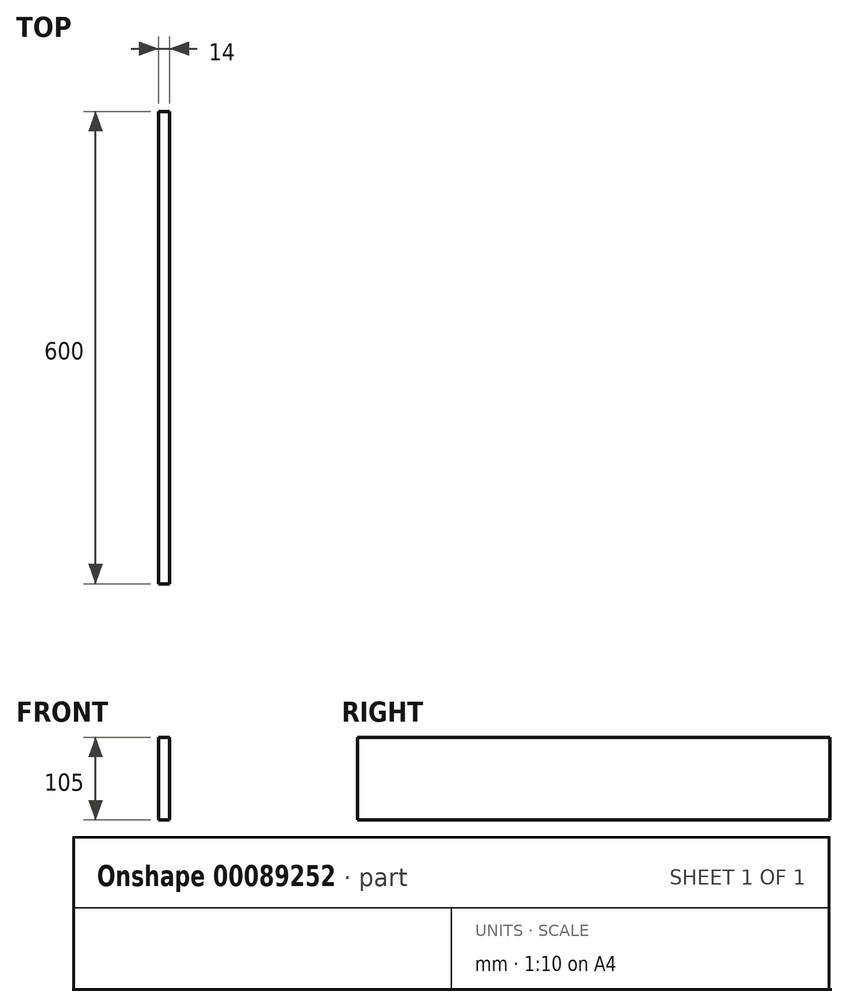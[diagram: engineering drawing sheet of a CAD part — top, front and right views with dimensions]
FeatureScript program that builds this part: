
annotation { "Feature Type Name" : "Feature", "Feature Type Description" : "" }
export const myFeature = defineFeature(function(context is Context, id is Id, definition is map)
    precondition{}
    {
        {
            var Q0;
            Q0=qCreatedBy(makeId("Front.planeOp"),FACE);
            var sketch = newSketch(context, id + "F0", { "sketchPlane" : qUnion([Q0])});
            skLineSegment(sketch, "E0.bottom", {"start": v(-7, 52.5) * mm, "end": v(7, 52.5) * mm});
            skLineSegment(sketch, "E0.top", {"start": v(-7, -52.5) * mm, "end": v(7, -52.5) * mm});
            skLineSegment(sketch, "E0.left", {"start": v(-7, 52.5) * mm, "end": v(-7, -52.5) * mm});
            skLineSegment(sketch, "E0.right", {"start": v(7, 52.5) * mm, "end": v(7, -52.5) * mm});
            skPoint(sketch, "E0.middle", {"position": v(0, 0) * mm});
            skSolve(sketch);
        }
        {
            var Q0;
            Q0=makeQuery(id+"F0.imprint","IMPRINT",FACE,{"disambiguationData":[TD([[makeQuery(id+"F0.imprint","IMPRINT",EDGE,{"derivedFrom":sQuery(id+"F0.wireOp",EDGE,"E0.bottom")}),-1.0]])]});
            extrude(context, id + "F1", {"entities" : qUnion([Q0]), "depth" : 600 * mm});
        }
    });
